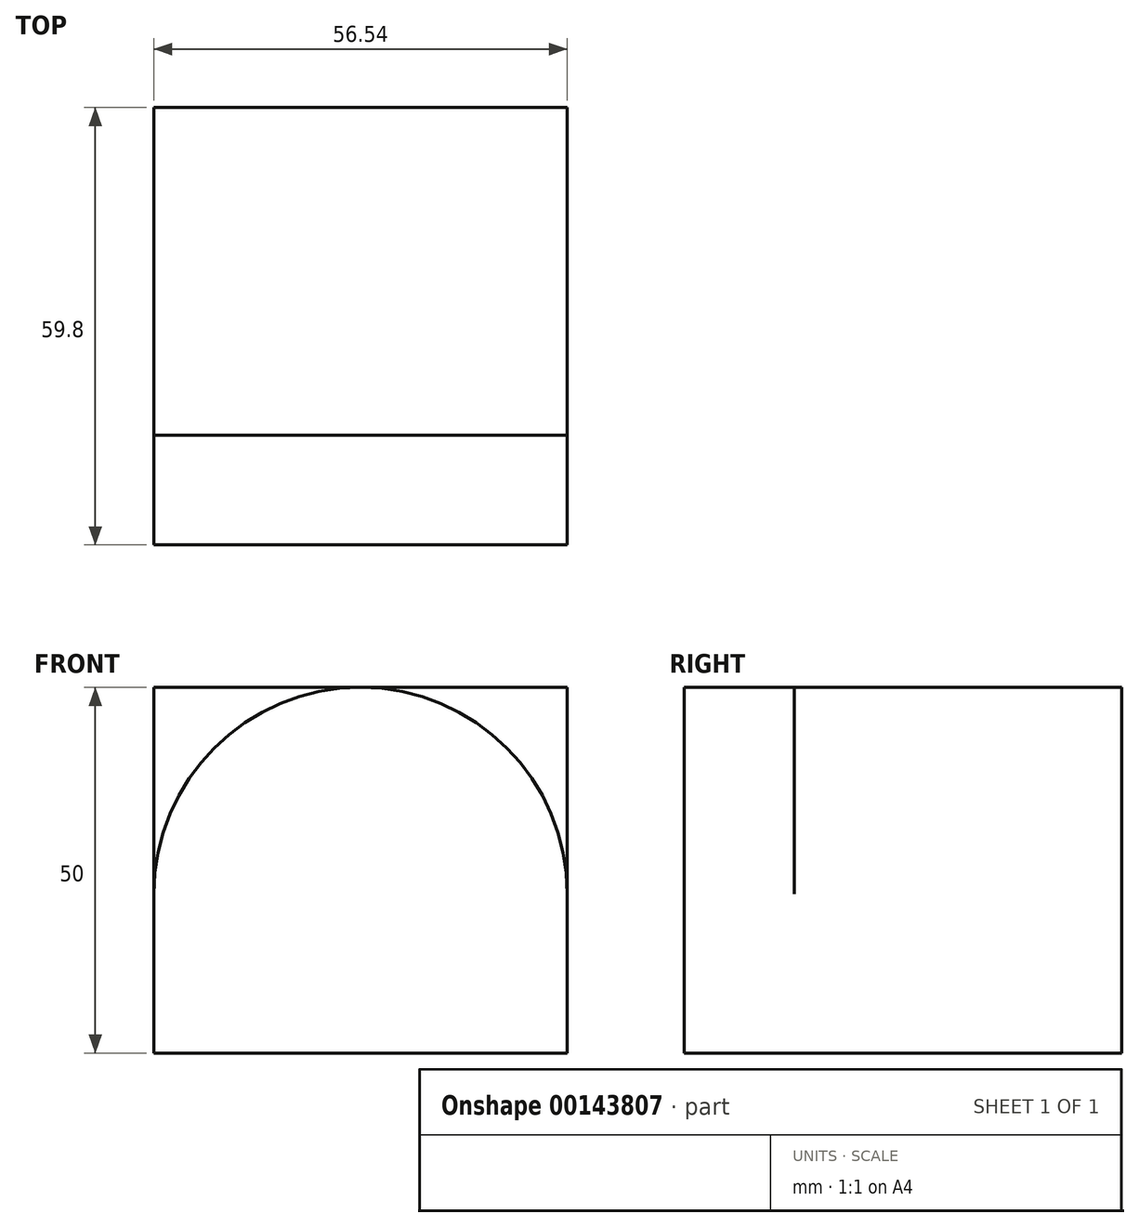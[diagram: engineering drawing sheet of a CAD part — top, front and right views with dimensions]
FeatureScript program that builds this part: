
annotation { "Feature Type Name" : "Feature", "Feature Type Description" : "" }
export const myFeature = defineFeature(function(context is Context, id is Id, definition is map)
    precondition{}
    {
        {
            var Q0;
            Q0=qCreatedBy(makeId("Top.planeOp"),FACE);
            var sketch = newSketch(context, id + "F0", { "sketchPlane" : qUnion([Q0])});
            skLineSegment(sketch, "E0.bottom", {"start": v(-28.27, 29.9) * mm, "end": v(28.27, 29.9) * mm});
            skLineSegment(sketch, "E0.top", {"start": v(-28.27, -29.9) * mm, "end": v(28.27, -29.9) * mm});
            skLineSegment(sketch, "E0.left", {"start": v(-28.27, 29.9) * mm, "end": v(-28.27, -29.9) * mm});
            skLineSegment(sketch, "E0.right", {"start": v(28.27, 29.9) * mm, "end": v(28.27, -29.9) * mm});
            skPoint(sketch, "E0.middle", {"position": v(0, 0) * mm});
            skSolve(sketch);
        }
        {
            var Q0;
            Q0 = qSketchRegion(id + "F0", true);
            extrude(context, id + "F1", {"entities" : qUnion([Q0]), "depth" : 50 * mm});
        }
        {
            var Q0;
            Q0=makeQuery(id+"F1.opExtrude","SWEPT_FACE",FACE,{"disambiguationData":[OSD([sQuery(id+"F0.wireOp",EDGE,"E0.top")])]});
            var sketch = newSketch(context, id + "F2", { "sketchPlane" : qUnion([Q0])});
            skCircle(sketch, "E1", {"center": v(0, 21.73) * mm, "radius": 28.27 * mm});
            skLineSegment(sketch, "E2", {"start": v(-28.27, 21.73) * mm, "end": v(28.27, 21.73) * mm});
            skSolve(sketch);
        }
        {
            var Q0;
            {var subQ0=sQuery(id+"F2.wireOp",EDGE,"E1");var subQ1=sQuery(id+"F0.wireOp",EDGE,"E0.top");var subQ4=makeQuery(id+"F1.opExtrude","CAP_EDGE",EDGE,{"disambiguationData":[OSD([subQ1])],"isStart":false});var subQ5=makeQuery(id+"F2.imprint","INTERSECT",VERTEX,{"derivedFrom":[subQ4,subQ0]});Q0=makeQuery(id+"F2.imprint","IMPRINT",FACE,{"disambiguationData":[TD([[makeQuery(id+"F2.imprint","IMPRINT",EDGE,{"disambiguationData":[TD([[subQ5,-1.0]])],"derivedFrom":subQ4}),-1.0]])]});}
            var Q1;
            {var subQ0=sQuery(id+"F2.wireOp",EDGE,"E1");var subQ1=sQuery(id+"F0.wireOp",EDGE,"E0.top");var subQ4=makeQuery(id+"F1.opExtrude","CAP_EDGE",EDGE,{"disambiguationData":[OSD([subQ1])],"isStart":false});var subQ5=makeQuery(id+"F2.imprint","INTERSECT",VERTEX,{"derivedFrom":[subQ4,subQ0]});Q1=makeQuery(id+"F2.imprint","IMPRINT",FACE,{"disambiguationData":[TD([[makeQuery(id+"F2.imprint","IMPRINT",EDGE,{"disambiguationData":[TD([[subQ5,1.0]])],"derivedFrom":subQ4}),-1.0]])]});}
            extrude(context, id + "F3", {"entities" : qUnion([Q0, Q1]), "operationType" : NewBodyOperationType.REMOVE, "oppositeDirection" : true, "depth" : 15 * mm});
        }
    });
